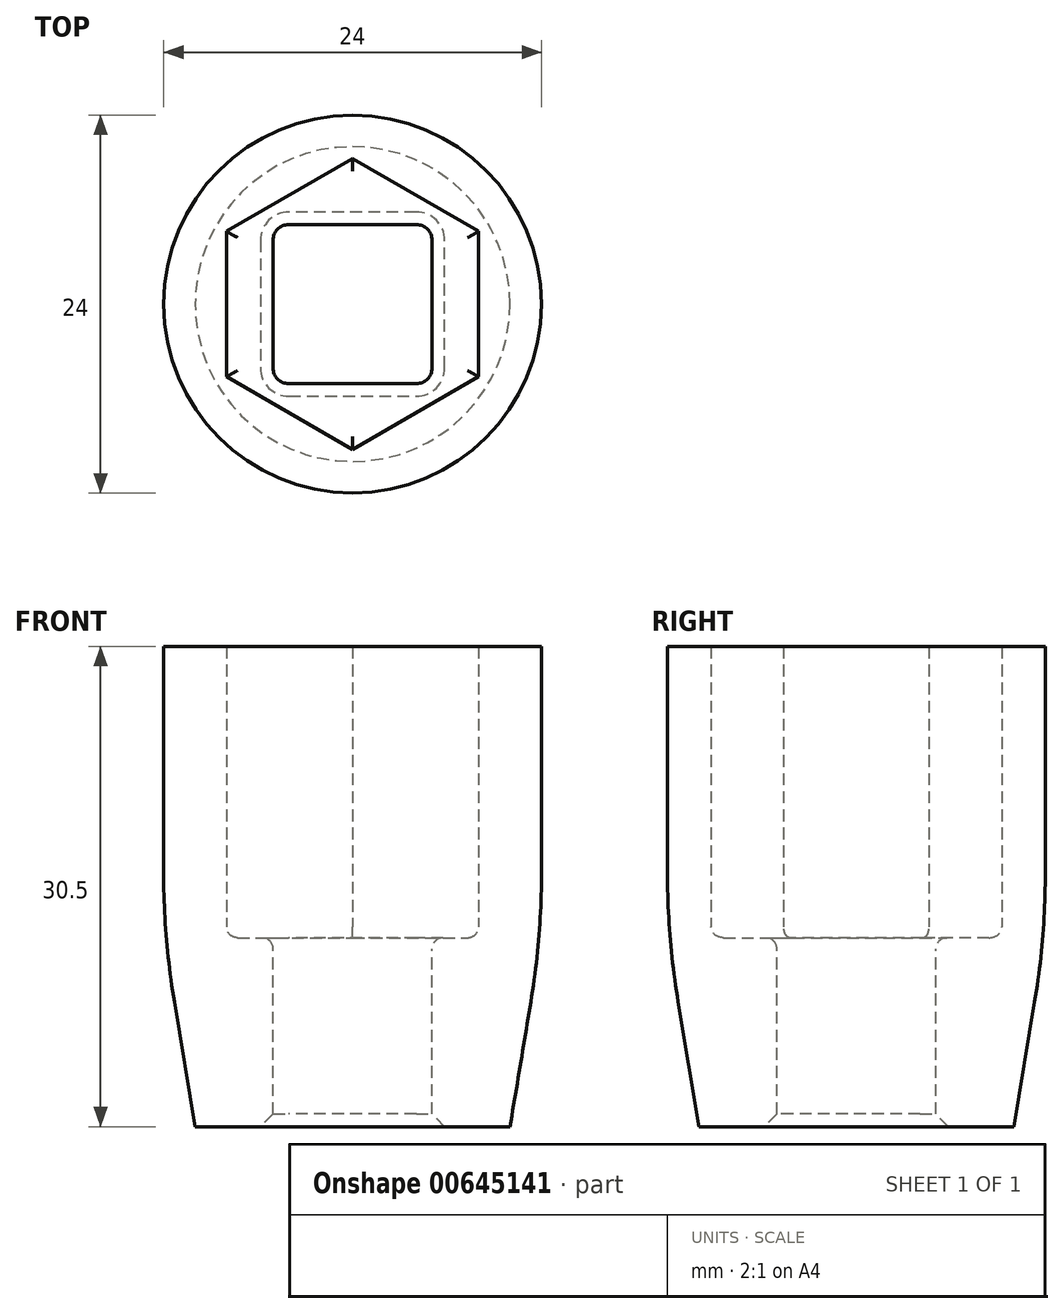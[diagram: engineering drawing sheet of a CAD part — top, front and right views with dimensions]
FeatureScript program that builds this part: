
annotation { "Feature Type Name" : "Feature", "Feature Type Description" : "" }
export const myFeature = defineFeature(function(context is Context, id is Id, definition is map)
    precondition{}
    {
        {
            var Q0;
            Q0=qCreatedBy(makeId("Top.planeOp"),FACE);
            var sketch = newSketch(context, id + "F0", { "sketchPlane" : qUnion([Q0])});
            skCircle(sketch, "E0.cCircle", {"center": v(0, 0) * mm, "radius": 8 * mm, "construction": true});
            skLineSegment(sketch, "E0.0", {"start": v(8, 4.62) * mm, "end": v(8, -4.62) * mm});
            skLineSegment(sketch, "E0.1", {"start": v(8, -4.62) * mm, "end": v(0, -9.24) * mm});
            skLineSegment(sketch, "E0.2", {"start": v(0, -9.24) * mm, "end": v(-8, -4.62) * mm});
            skLineSegment(sketch, "E0.3", {"start": v(-8, -4.62) * mm, "end": v(-8, 4.62) * mm});
            skLineSegment(sketch, "E0.4", {"start": v(-8, 4.62) * mm, "end": v(0, 9.24) * mm});
            skLineSegment(sketch, "E0.5", {"start": v(0, 9.24) * mm, "end": v(8, 4.62) * mm});
            skPoint(sketch, "E0.0.midPoint", {"position": v(8, 0) * mm});
            skCircle(sketch, "E1", {"center": v(0, 0) * mm, "radius": 12 * mm});
            skLineSegment(sketch, "E2.bottom", {"start": v(5.05, -5.05) * mm, "end": v(-5.05, -5.05) * mm});
            skLineSegment(sketch, "E2.top", {"start": v(5.05, 5.05) * mm, "end": v(-5.05, 5.05) * mm});
            skLineSegment(sketch, "E2.left", {"start": v(5.05, -5.05) * mm, "end": v(5.05, 5.05) * mm});
            skLineSegment(sketch, "E2.right", {"start": v(-5.05, -5.05) * mm, "end": v(-5.05, 5.05) * mm});
            skSolve(sketch);
        }
        {
            var Q0;
            {var subQ5=sQuery(id+"F0.wireOp",EDGE,"E0.0");Q0=makeQuery(id+"F0.imprint","IMPRINT",FACE,{"disambiguationData":[TD([[makeQuery(id+"F0.imprint","IMPRINT",EDGE,{"derivedFrom":subQ5}),1.0]])]});}
            var Q1;
            Q1=makeQuery(id+"F0.imprint","IMPRINT",FACE,{"disambiguationData":[TD([[makeQuery(id+"F0.imprint","IMPRINT",EDGE,{"derivedFrom":sQuery(id+"F0.wireOp",EDGE,"E1")}),-1.0]])]});
            extrude(context, id + "F1", {"entities" : qUnion([Q0, Q1]), "depth" : 18.5 * mm, "offsetDistance" : 25 * mm});
        }
        {
            var Q0;
            Q0=makeQuery(id+"F0.imprint","IMPRINT",FACE,{"disambiguationData":[TD([[makeQuery(id+"F0.imprint","IMPRINT",EDGE,{"derivedFrom":sQuery(id+"F0.wireOp",EDGE,"E0.0")}),-1.0]])]});
            var Q1;
            Q1=makeQuery(id+"F0.imprint","IMPRINT",FACE,{"disambiguationData":[TD([[makeQuery(id+"F0.imprint","IMPRINT",EDGE,{"derivedFrom":sQuery(id+"F0.wireOp",EDGE,"E0.0")}),1.0]])]});
            extrude(context, id + "F2", {"entities" : qUnion([Q0, Q1]), "operationType" : NewBodyOperationType.ADD, "oppositeDirection" : true, "depth" : 12 * mm, "offsetDistance" : 25 * mm});
        }
        {
            var Q0;
            Q0=makeQuery(id+"F2.opExtrude","CAP_EDGE",EDGE,{"disambiguationData":[OSD([sQuery(id+"F0.wireOp",EDGE,"E1")])],"isStart":false});
            chamfer(context, id + "F3", {"entities" : qUnion([Q0]), "chamferType" : ChamferType.TWO_OFFSETS, "width1" : 2 * mm, "oppositeDirection" : true, "width2" : 12 * mm, "tangentPropagation" : true});
        }
        {
            var Q0;
            Q0=makeQuery(id+"F2.opExtrude","SWEPT_EDGE",EDGE,{"disambiguationData":[OSD([sQuery(id+"F0.wireOp",EDGE,"E2.top"),sQuery(id+"F0.wireOp",EDGE,"E2.right")])]});
            var Q1;
            Q1=makeQuery(id+"F2.opExtrude","SWEPT_EDGE",EDGE,{"disambiguationData":[OSD([sQuery(id+"F0.wireOp",EDGE,"E2.top"),sQuery(id+"F0.wireOp",EDGE,"E2.left")])]});
            var Q2;
            Q2=makeQuery(id+"F2.opExtrude","SWEPT_EDGE",EDGE,{"disambiguationData":[OSD([sQuery(id+"F0.wireOp",EDGE,"E2.bottom"),sQuery(id+"F0.wireOp",EDGE,"E2.left")])]});
            var Q3;
            Q3=makeQuery(id+"F2.opExtrude","SWEPT_EDGE",EDGE,{"disambiguationData":[OSD([sQuery(id+"F0.wireOp",EDGE,"E2.bottom"),sQuery(id+"F0.wireOp",EDGE,"E2.right")])]});
            fillet(context, id + "F4", {"entities" : qUnion([Q0, Q1, Q2, Q3]), "tangentPropagation" : true, "radius" : 1 * mm, "defaultsChanged" : false, "vertexSettings" : [], "allowEdgeOverflow" : false});
        }
        {
            var Q0;
            Q0=makeQuery(id+"F1.opExtrude","CAP_EDGE",EDGE,{"disambiguationData":[OSD([sQuery(id+"F0.wireOp",EDGE,"E0.1")])],"isStart":true});
            var Q1;
            Q1=makeQuery(id+"F1.opExtrude","CAP_EDGE",EDGE,{"disambiguationData":[OSD([sQuery(id+"F0.wireOp",EDGE,"E0.2")])],"isStart":true});
            var Q2;
            Q2=makeQuery(id+"F2.opExtrude","CAP_FACE",FACE,{"disambiguationData":[OSD([sQuery(id+"F0.wireOp",EDGE,"E1"),sQuery(id+"F0.wireOp",EDGE,"E2.bottom"),sQuery(id+"F0.wireOp",EDGE,"E2.top"),sQuery(id+"F0.wireOp",EDGE,"E2.left"),sQuery(id+"F0.wireOp",EDGE,"E2.right")])],"isStart":true});
            fillet(context, id + "F5", {"entities" : qUnion([Q0, Q1, Q2]), "radius" : 0.7 * mm, "tangentPropagation" : true, "defaultsChanged" : true, "vertexSettings" : [], "allowEdgeOverflow" : false});
        }
        {
            var Q0;
            {var subQ0=sQuery(id+"F0.wireOp",EDGE,"E1");Q0=makeQuery(id+"F3.opChamfer","BLEND_EDGE",EDGE,{"blendedFrom":[makeQuery(id+"F2.opExtrude","CAP_EDGE",EDGE,{"disambiguationData":[OSD([subQ0])],"isStart":false}),makeQuery(id+"F2.boolean.opBoolean","MERGE",FACE,{"derivedFrom":[makeQuery(id+"F1.opExtrude","SWEPT_FACE",FACE,{"disambiguationData":[OSD([subQ0])]}),makeQuery(id+"F2.opExtrude","SWEPT_FACE",FACE,{"disambiguationData":[OSD([subQ0])]})]})],"blendedInto":[makeQuery(id+"F2.boolean.opBoolean","MERGE",FACE,{"derivedFrom":[makeQuery(id+"F1.opExtrude","SWEPT_FACE",FACE,{"disambiguationData":[OSD([subQ0])]}),makeQuery(id+"F2.opExtrude","SWEPT_FACE",FACE,{"disambiguationData":[OSD([subQ0])]})]})]});}
            fillet(context, id + "F6", {"entities" : qUnion([Q0]), "tangentPropagation" : true, "radius" : 50 * mm, "defaultsChanged" : true, "vertexSettings" : [], "allowEdgeOverflow" : false});
        }
        {
            var Q0;
            Q0=makeQuery(id+"F2.opExtrude","CAP_EDGE",EDGE,{"disambiguationData":[OSD([sQuery(id+"F0.wireOp",EDGE,"E2.left")])],"isStart":false});
            chamfer(context, id + "F7", {"entities" : qUnion([Q0]), "width" : 0.8 * mm, "tangentPropagation" : true});
        }
    });
